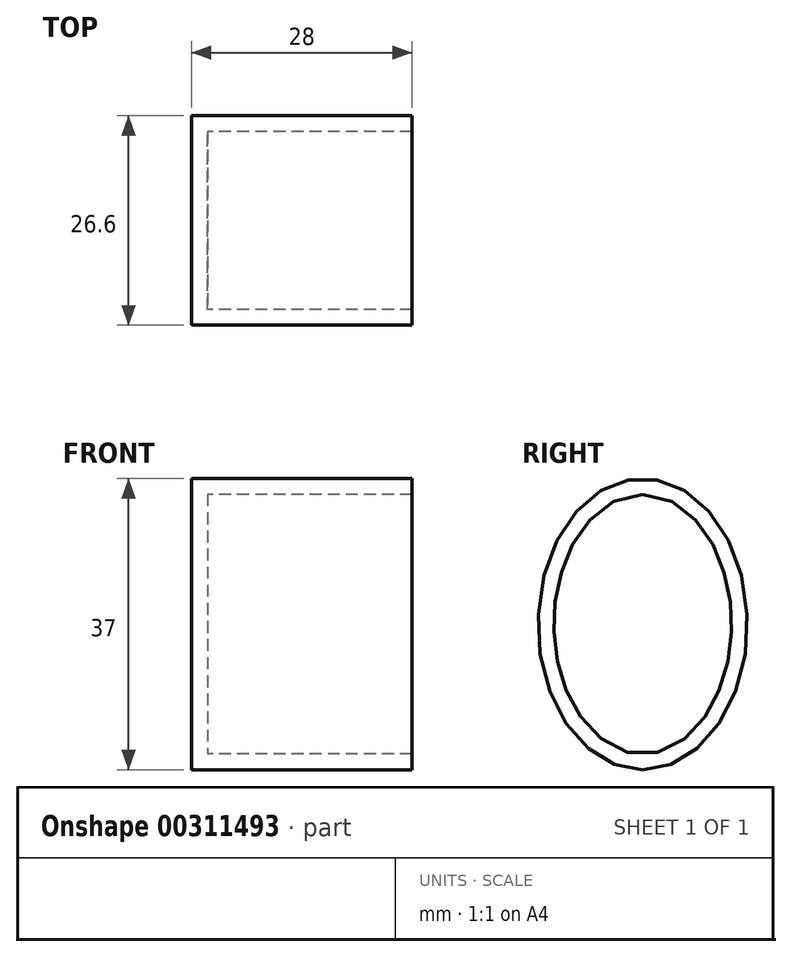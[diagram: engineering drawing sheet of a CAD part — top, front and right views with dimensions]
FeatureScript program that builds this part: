
annotation { "Feature Type Name" : "Feature", "Feature Type Description" : "" }
export const myFeature = defineFeature(function(context is Context, id is Id, definition is map)
    precondition{}
    {
        {
            var Q0;
            Q0=qCreatedBy(makeId("Right.planeOp"),FACE);
            var sketch = newSketch(context, id + "F0", { "sketchPlane" : qUnion([Q0])});
            skEllipse(sketch, "E0", {"center": v(0, 0) * mm, "majorRadius": 18.5 * mm, "minorRadius": 13.3 * mm, "majorAxis": v(0, -1)});
            skSolve(sketch);
        }
        {
            var Q0;
            Q0=makeQuery(id+"F0.imprint","IMPRINT",FACE,{"disambiguationData":[TD([[makeQuery(id+"F0.imprint","IMPRINT",EDGE,{"derivedFrom":sQuery(id+"F0.wireOp",EDGE,"E0")}),1.0]])]});
            var Q1;
            Q1=sQuery(id+"F0.wireOp",EDGE,"E0");
            extrude(context, id + "F1", {"entities" : qUnion([Q0]), "surfaceEntities" : qUnion([Q1]), "depth" : 28 * mm});
        }
        {
            var Q0;
            Q0=makeQuery(id+"F1.opExtrude","CAP_FACE",FACE,{"disambiguationData":[OSD([sQuery(id+"F0.wireOp",EDGE,"E0")])],"isStart":false});
            shell(context, id + "F2", {"entities" : qUnion([Q0]), "thickness" : 2 * mm});
        }
    });
